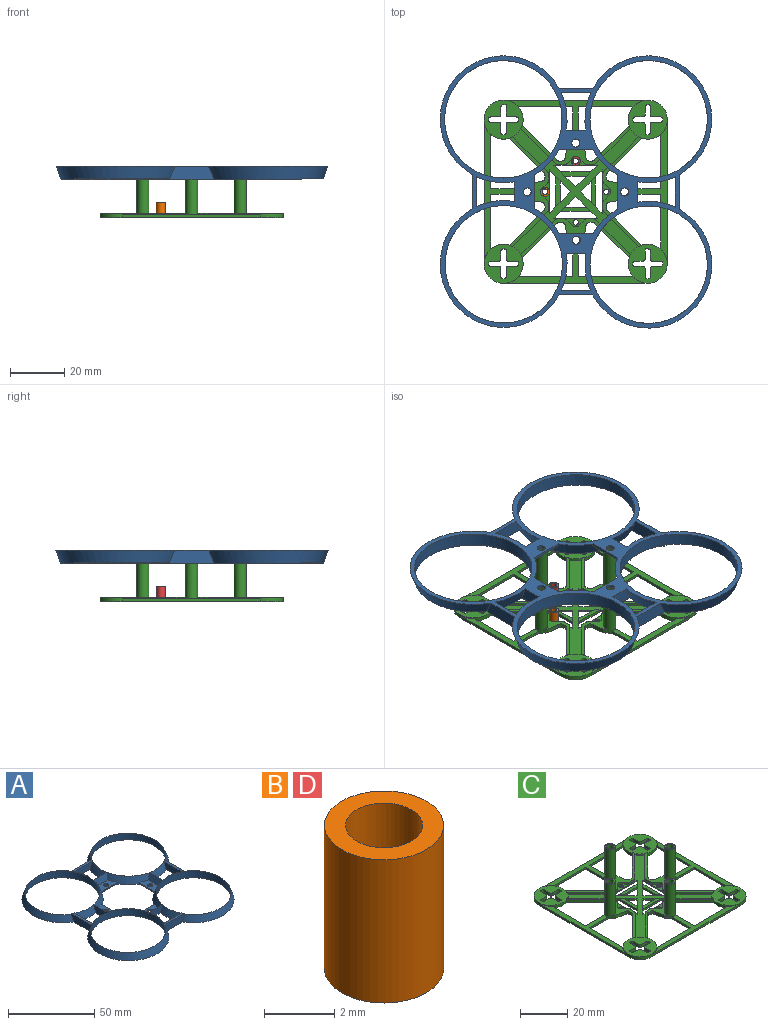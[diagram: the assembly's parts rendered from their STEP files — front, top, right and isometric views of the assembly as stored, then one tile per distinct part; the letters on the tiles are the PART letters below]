
ASSEMBLY  parts=4 mates=3
PART A: 54 faces, bbox 100.6x100.9x5.1 mm
  f0: cylinder r=21.74mm len=43.48mm, axis (0,0,-1), area 657.2mm2, adj f7,f11,f12,f13,f21,f22,f28,f36
  f1: cylinder r=21.74mm len=43.48mm, axis (0,0,-1), area 657.2mm2, adj f5,f6,f7,f8,f9,f17,f25,f26
  f2: cylinder r=21.74mm len=43.48mm, axis (0,0,-1), area 657.2mm2, adj f8,f9,f10,f17,f18,f24,f25,f27
  f3: cylinder r=21.74mm len=43.48mm, axis (0,0,-1), area 657.2mm2, adj f4,f10,f19,f20,f30,f31,f35,f36
  f4: cone r=23.5mm half-angle=20deg, axis (0,0,-1), area 121.3mm2, adj f3,f36,f37,f45,f46,f47,f49,f50
  f5: cone r=23.5mm half-angle=20deg, axis (0,0,-1), area 416mm2, adj f1,f7,f17,f23,f37
  f6: cone r=23.5mm half-angle=20deg, axis (0,0,-1), area 121.3mm2, adj f1,f7,f37,f38,f40,f41,f43,f51
  f7: plane 38.68x36.77mm, normal (0,0,1), area 28.4mm2, adj f0,f1,f5,f6,f14,f15,f16,f22
  f8: plane 16.71x1.51mm, normal (0,0,1), area 23.9mm2, adj f1,f2,f17,f25
  f9: plane 11.13x0.1mm, normal (0,0,1), area 1.1mm2, adj f1,f2,f34,f53
  f10: plane 36.77x27.56mm, normal (0,0,1), area 26.3mm2, adj f2,f3,f18,f19,f27,f29,f30,f35
  f11: plane 10.91x5.01mm, normal (1,0,0), area 45.5mm2, adj f0,f12,f32,f36,f37
  f12: cone r=23.5mm half-angle=20deg, axis (0,0,-1), area 72.2mm2, adj f0,f11,f13,f37
  f13: plane 14.95x5.04mm, normal (-1,0,0), area 65.1mm2, adj f0,f12,f32,f36,f37
  f14: plane 10.97x5.01mm, normal (0,1,0), area 45.5mm2, adj f7,f15,f33,f37
  f15: cone r=23.5mm half-angle=20deg, axis (0,0,-1), area 76.1mm2, adj f7,f14,f16,f37
  f16: plane 15.09x5.04mm, normal (0,-1,0), area 65.1mm2, adj f7,f15,f33,f37
  f17: plane 16.75x5.04mm, normal (-1,0,0), area 74.4mm2, adj f1,f2,f5,f8,f18,f37
  f18: cone r=23.5mm half-angle=20deg, axis (0,0,-1), area 417.6mm2, adj f2,f10,f17,f19,f37
  f19: plane 16.5x5.05mm, normal (0,-1,0), area 72.5mm2, adj f3,f10,f18,f20,f37
  f20: cone r=23.5mm half-angle=20deg, axis (0,0,-1), area 416mm2, adj f3,f19,f21,f36,f37
  f21: plane 16.66x5.05mm, normal (1,0,0), area 73.2mm2, adj f0,f20,f22,f36,f37
  f22: cone r=23.5mm half-angle=20deg, axis (0,0,-1), area 416mm2, adj f0,f7,f21,f23,f37
  f23: plane 16.82x5.05mm, normal (0,1,0), area 73.2mm2, adj f5,f7,f22,f37
  f24: cone r=23.5mm half-angle=20deg, axis (0,0,-1), area 72.2mm2, adj f2,f25,f34,f37
  f25: plane 15.06x5.03mm, normal (1,0,0), area 66.3mm2, adj f1,f2,f8,f24,f26,f37
  f26: cone r=23.5mm half-angle=20deg, axis (0,0,-1), area 72.2mm2, adj f1,f25,f34,f37
  f27: cone r=23.5mm half-angle=20deg, axis (0,0,-1), area 119.8mm2, adj f2,f10,f37,f38,f40,f45,f46,f52
  f28: cone r=23.5mm half-angle=20deg, axis (0,0,-1), area 121.3mm2, adj f0,f7,f37,f41,f43,f47,f49,f50
  f29: cone r=23.5mm half-angle=20deg, axis (0,0,-1), area 75.9mm2, adj f10,f30,f35,f37
  f30: plane 10.96x5.01mm, normal (0,-1,0), area 45.8mm2, adj f3,f10,f29,f31,f37
  f31: cone r=23.5mm half-angle=20deg, axis (0,0,-1), area 72.2mm2, adj f3,f30,f35,f37
  f32: cone r=23.5mm half-angle=20deg, axis (0,0,-1), area 76.1mm2, adj f11,f13,f36,f37
  f33: cone r=23.5mm half-angle=20deg, axis (0,0,-1), area 76.1mm2, adj f7,f14,f16,f37
  f34: plane 11.11x5.01mm, normal (-1,0,0), area 46.8mm2, adj f1,f2,f9,f24,f26,f37
  f35: plane 14.82x5.04mm, normal (0,1,0), area 64.5mm2, adj f3,f10,f29,f31,f37
  f36: plane 36.77x27.56mm, normal (0,0,1), area 26.5mm2, adj f0,f3,f4,f11,f13,f20,f21,f32
  f37: plane 100.84x100.59mm, normal (0,0,-1), area 1324.1mm2, adj f0,f1,f2,f3,f4,f5,f6,f11
  f38: plane 13.52x1mm, normal (1,0,0), area 13.1mm2, adj f6,f27,f37,f40
  f39: cylinder r=1.5mm len=3mm, axis (0,0,-1), area 9.4mm2, adj f37,f40
  f40: plane 13.52x5.75mm, normal (0,0,1), area 55.8mm2, adj f6,f27,f38,f39,f53
  f41: plane 13.26x1mm, normal (0,-1,0), area 12.8mm2, adj f6,f28,f37,f43
  f42: cylinder r=1.5mm len=3mm, axis (0,0,-1), area 9.4mm2, adj f37,f43
  f43: plane 13.26x5.75mm, normal (0,0,1), area 54.3mm2, adj f6,f28,f41,f42,f51
  f44: cylinder r=1.5mm len=3mm, axis (0,0,-1), area 9.4mm2, adj f37,f46
  f45: plane 13.41x1mm, normal (0,1,0), area 13mm2, adj f4,f27,f37,f46
  f46: plane 13.41x5.75mm, normal (0,0,1), area 54.9mm2, adj f4,f27,f44,f45,f52
  f47: plane 13.26x1mm, normal (-1,0,0), area 12.8mm2, adj f4,f28,f37,f49
  f48: cylinder r=1.5mm len=3mm, axis (0,0,-1), area 9.4mm2, adj f37,f49
  f49: plane 13.26x5.75mm, normal (0,0,1), area 54.3mm2, adj f4,f28,f47,f48,f50
  f50: plane 11.01x4.06mm, normal (-0.93,0,0.36), area 42.1mm2, adj f0,f4,f28,f36,f49
  f51: plane 11.05x4.06mm, normal (0,-0.93,0.36), area 42.1mm2, adj f6,f7,f28,f43
  f52: plane 11.06x4.06mm, normal (0,0.93,0.36), area 42.4mm2, adj f3,f4,f10,f27,f46
  f53: plane 11.21x4.05mm, normal (0.93,0,0.36), area 43.2mm2, adj f1,f2,f6,f9,f27,f40
PART B: 4 faces, bbox 3.4x3.4x5 mm
  f0: cylinder r=1.1mm len=5mm, axis (0,0,-1), area 34.6mm2, adj f2,f3
  f1: cylinder r=1.7mm len=5mm, axis (0,0,-1), area 53.4mm2, adj f2,f3
  f2: plane 3.4x3.4mm, normal (0,0,1), area 5.3mm2, adj f0,f1
  f3: plane 3.4x3.4mm, normal (0,0,-1), area 5.3mm2, adj f0,f1
PART C: 299 faces, bbox 67.8x67.8x18 mm
  f0: cylinder r=7.23mm len=14.46mm, axis (0,0,-1), area 47.5mm2, adj f33,f70,f77,f94,f275,f276,f280,f282
  f1: cylinder r=2.25mm len=18mm, axis (0,0,-1), area 237.7mm2, adj f32,f36,f37,f77,f78,f281,f285,f286
  f2: plane 4.02x4.02mm, normal (0.71,0.71,0), area 3.4mm2, adj f11,f77,f165,f272
  f3: plane 2.5x2.5mm, normal (0.71,-0.71,0), area 2.1mm2, adj f22,f77,f165,f273
  f4: plane 2.5x2.5mm, normal (-0.71,-0.71,0), area 2.1mm2, adj f13,f77,f165,f268
  f5: plane 4.02x4.02mm, normal (0.71,-0.71,0), area 3.4mm2, adj f12,f77,f165,f267
  f6: plane 2.5x2.5mm, normal (-0.71,0.71,0), area 2.1mm2, adj f17,f77,f165,f263
  f7: plane 4.02x4.02mm, normal (-0.71,-0.71,0), area 3.4mm2, adj f16,f77,f165,f262
  f8: plane 2.5x2.5mm, normal (-0.71,0.71,0), area 2.1mm2, adj f27,f77,f165,f258
  f9: plane 4.02x4.02mm, normal (0.71,0.71,0), area 3.4mm2, adj f14,f77,f165,f257
  f10: plane 2.5x2.5mm, normal (0.71,0.71,0), area 2.1mm2, adj f22,f77,f165,f273
  f11: plane 4.02x4.02mm, normal (0.71,-0.71,0), area 3.4mm2, adj f2,f77,f165,f272
  f12: plane 4.02x4.02mm, normal (-0.71,-0.71,0), area 3.4mm2, adj f5,f77,f165,f267
  f13: plane 16.1x0.6mm, normal (0,1,0), area 9.7mm2, adj f4,f26,f77,f165
  f14: plane 4.02x4.02mm, normal (-0.71,0.71,0), area 3.4mm2, adj f9,f77,f165,f257
  f15: plane 2.5x2.5mm, normal (0.71,0.71,0), area 2.1mm2, adj f27,f77,f165,f258
  f16: plane 4.02x4.02mm, normal (-0.71,0.71,0), area 3.4mm2, adj f7,f77,f165,f262
  f17: plane 16.1x0.6mm, normal (1,0,0), area 9.7mm2, adj f6,f28,f77,f165
  f18: cylinder r=7.23mm len=1.16mm, axis (0,0,-1), area 0.1mm2, adj f42,f76,f122,f158
  f19: cylinder r=7.23mm len=1.19mm, axis (0,0,-1), area 0.1mm2, adj f30,f52,f136,f137
  f20: cylinder r=7.23mm len=1.16mm, axis (0,0,-1), area 0.1mm2, adj f31,f62,f108,f144
  f21: cylinder r=1mm len=2mm, axis (0,0,-1), area 3.8mm2, adj f77,f165
  f22: plane 16.1x0.6mm, normal (-1,0,0), area 9.7mm2, adj f3,f10,f77,f165
  f23: cylinder r=1mm len=2mm, axis (0,0,-1), area 3.8mm2, adj f77,f165
  f24: cylinder r=1mm len=2mm, axis (0,0,-1), area 3.8mm2, adj f77,f165
  f25: cylinder r=1mm len=2mm, axis (0,0,-1), area 3.8mm2, adj f77,f165
  f26: plane 2.5x2.5mm, normal (0.71,-0.71,0), area 2.1mm2, adj f13,f77,f165,f268
  f27: plane 16.1x0.6mm, normal (0,-1,0), area 9.7mm2, adj f8,f15,f77,f165
  f28: plane 2.5x2.5mm, normal (-0.71,-0.71,0), area 2.1mm2, adj f17,f77,f165,f263
  f29: cylinder r=7.23mm len=1.19mm, axis (0,0,-1), area 0.1mm2, adj f31,f70,f94,f149
  f30: plane 40.62x14.52mm, normal (0,0,1), area 90.9mm2, adj f19,f52,f53,f54,f55,f56,f57,f58
  f31: plane 40.61x14.49mm, normal (0,0,1), area 89.8mm2, adj f20,f29,f62,f63,f64,f65,f66,f67
  f32: plane 40.61x14.52mm, normal (0,0,1), area 91mm2, adj f1,f33,f34,f35,f36,f37,f38,f39
  f33: plane 12.73x12.73mm, normal (-0.71,-0.71,0), area 28.8mm2, adj f0,f32,f74,f77,f186
  f34: plane 1.6x0.71mm, normal (-1,0,0), area 1.1mm2, adj f32,f77,f186,f187
  f35: plane 4.91x1.6mm, normal (-0.15,0.99,0), area 7.9mm2, adj f32,f77,f187,f191
  f36: plane 1.6x0.64mm, normal (-0.71,0.7,0), area 1.4mm2, adj f1,f32,f77,f191
  f37: plane 1.6x0.64mm, normal (-0.71,-0.7,0), area 1.4mm2, adj f1,f32,f77,f192
  f38: plane 4.91x1.6mm, normal (-0.15,-0.99,0), area 7.9mm2, adj f32,f77,f192,f193
  f39: plane 1.6x0.71mm, normal (-1,0,0), area 1.1mm2, adj f32,f77,f193,f194
  f40: plane 12.73x12.73mm, normal (-0.71,0.71,0), area 28.8mm2, adj f32,f41,f77,f109,f194
  f41: cylinder r=7.23mm len=1.23mm, axis (0,0,-1), area 0.1mm2, adj f32,f40,f122,f156
  f42: plane 12.7x12.7mm, normal (0.71,-0.71,0), area 28.7mm2, adj f18,f76,f77,f109,f195
  f43: plane 1.6x0.76mm, normal (0,-1,0), area 1.2mm2, adj f76,f77,f195,f196
  f44: plane 4.91x1.6mm, normal (-0.99,-0.15,0), area 7.9mm2, adj f76,f77,f196,f197
  f45: plane 1.6x0.64mm, normal (-0.7,-0.71,0), area 1.4mm2, adj f46,f76,f77,f197
  f46: cylinder r=2.25mm len=18mm, axis (0,0,-1), area 237.7mm2, adj f45,f47,f76,f77,f81,f293,f297,f298
  f47: plane 1.6x0.64mm, normal (0.7,-0.71,0), area 1.4mm2, adj f46,f76,f77,f198
  f48: plane 4.91x1.6mm, normal (0.99,-0.15,0), area 7.9mm2, adj f76,f77,f198,f199
  f49: plane 1.6x0.71mm, normal (0,-1,0), area 1.1mm2, adj f76,f77,f199,f200
  f50: plane 12.73x12.73mm, normal (-0.71,-0.71,0), area 28.8mm2, adj f51,f76,f77,f123,f200
  f51: cylinder r=7.23mm len=1.2mm, axis (0,0,-1), area 0.1mm2, adj f50,f76,f136,f163
  f52: plane 12.7x12.7mm, normal (0.71,0.71,0), area 28.7mm2, adj f19,f30,f77,f123,f201
  f53: plane 1.6x0.76mm, normal (1,0,0), area 1.2mm2, adj f30,f77,f201,f207
  f54: plane 4.91x1.6mm, normal (0.15,-0.99,0), area 7.9mm2, adj f30,f77,f207,f208
  f55: plane 1.6x0.64mm, normal (0.71,-0.7,0), area 1.4mm2, adj f30,f56,f77,f208
  f56: cylinder r=2.25mm len=18mm, axis (0,0,-1), area 237.7mm2, adj f30,f55,f57,f77,f80,f287,f291,f292
  f57: plane 1.6x0.64mm, normal (0.71,0.7,0), area 1.4mm2, adj f30,f56,f77,f206
  f58: plane 4.91x1.6mm, normal (0.15,0.99,0), area 7.9mm2, adj f30,f77,f205,f206
  f59: plane 1.6x0.71mm, normal (1,0,0), area 1.1mm2, adj f30,f77,f190,f205
  f60: plane 12.73x12.73mm, normal (0.71,-0.71,0), area 28.8mm2, adj f30,f61,f77,f95,f190
  f61: cylinder r=7.23mm len=1.23mm, axis (0,0,-1), area 0.1mm2, adj f30,f60,f108,f142
  f62: plane 12.7x12.7mm, normal (-0.71,0.71,0), area 28.7mm2, adj f20,f31,f77,f95,f189
  f63: plane 1.6x0.76mm, normal (0,1,0), area 1.2mm2, adj f31,f77,f189,f203
  f64: plane 4.91x1.6mm, normal (0.99,0.15,0), area 7.9mm2, adj f31,f77,f203,f204
  f65: plane 1.6x0.64mm, normal (0.7,0.71,0), area 1.4mm2, adj f31,f66,f77,f204
  f66: cylinder r=2.25mm len=18mm, axis (0,0,-1), area 237.7mm2, adj f31,f65,f67,f77,f79,f277,f278,f280
  f67: plane 1.6x0.64mm, normal (-0.7,0.71,0), area 1.4mm2, adj f31,f66,f77,f202
  f68: plane 4.91x1.6mm, normal (-0.99,0.15,0), area 7.9mm2, adj f31,f77,f188,f202
  f69: plane 1.6x0.76mm, normal (0,1,0), area 1.2mm2, adj f31,f77,f185,f188
  f70: plane 12.7x12.7mm, normal (0.71,0.71,0), area 28.7mm2, adj f0,f29,f31,f77,f185
  f71: cylinder r=1.5mm len=18mm, axis (0,0,-1), area 169.6mm2, adj f77,f79
  f72: cylinder r=1.5mm len=18mm, axis (0,0,-1), area 169.6mm2, adj f77,f81
  f73: cylinder r=1.5mm len=18mm, axis (0,0,-1), area 169.6mm2, adj f77,f80
  f74: cylinder r=7.23mm len=1.2mm, axis (0,0,-1), area 0.1mm2, adj f32,f33,f94,f151
  f75: cylinder r=1.5mm len=18mm, axis (0,0,-1), area 169.6mm2, adj f77,f78
  f76: plane 40.59x14.52mm, normal (0,0,1), area 89.6mm2, adj f18,f42,f43,f44,f45,f46,f47,f48
  f77: plane 67.84x67.84mm, normal (0,0,-1), area 1962.7mm2, adj f0,f1,f2,f3,f4,f5,f6,f7
  f78: plane 4.5x4.5mm, normal (0,0,1), area 8.8mm2, adj f1,f75
  f79: plane 4.5x4.5mm, normal (0,0,1), area 8.8mm2, adj f66,f71
  f80: plane 4.5x4.5mm, normal (0,0,1), area 8.8mm2, adj f56,f73
  f81: plane 4.5x4.5mm, normal (0,0,1), area 8.8mm2, adj f46,f72
  f82: plane 3.1x1.5mm, normal (0,1,0), area 4.6mm2, adj f77,f94,f209,f219
  f83: plane 3.1x1.5mm, normal (-1,0,0), area 4.6mm2, adj f77,f94,f218,f219
  f84: plane 1.5x0.6mm, normal (0,1,0), area 0.9mm2, adj f77,f94,f217,f218
  f85: plane 3.1x1.5mm, normal (1,0,0), area 4.6mm2, adj f77,f94,f216,f217
  f86: plane 3.1x1.5mm, normal (0,1,0), area 4.7mm2, adj f77,f94,f215,f216
  f87: plane 1.5x0.6mm, normal (1,0,0), area 0.9mm2, adj f77,f94,f214,f215
  f88: plane 3.1x1.5mm, normal (0,-1,0), area 4.7mm2, adj f77,f94,f213,f214
  f89: plane 3.1x1.5mm, normal (1,0,0), area 4.7mm2, adj f77,f94,f212,f213
  f90: plane 1.5x1.3mm, normal (0,-1,0), area 2mm2, adj f77,f91,f94,f212
  f91: plane 3.8x1.5mm, normal (-1,0,0), area 5.7mm2, adj f77,f90,f94,f211
  f92: plane 3.1x1.5mm, normal (0,-1,0), area 4.6mm2, adj f77,f94,f210,f211
  f93: plane 1.5x0.6mm, normal (-1,0,0), area 0.9mm2, adj f77,f94,f209,f210
  f94: plane 14.46x14.46mm, normal (0,0,1), area 124.5mm2, adj f0,f29,f74,f82,f83,f84,f85,f86
  f95: cylinder r=7.23mm len=14.46mm, axis (0,0,-1), area 47.5mm2, adj f60,f62,f77,f108,f275,f279,f280,f289
  f96: plane 3.1x1.5mm, normal (1,0,0), area 4.6mm2, adj f77,f108,f220,f231
  f97: plane 3.1x1.5mm, normal (0,1,0), area 4.6mm2, adj f77,f108,f230,f231
  f98: plane 1.5x0.6mm, normal (1,0,0), area 0.9mm2, adj f77,f108,f229,f230
  f99: plane 3.1x1.5mm, normal (0,-1,0), area 4.6mm2, adj f77,f108,f228,f229
  f100: plane 3.1x1.5mm, normal (1,0,0), area 4.7mm2, adj f77,f108,f227,f228
  f101: plane 1.5x0.6mm, normal (0,-1,0), area 0.9mm2, adj f77,f108,f226,f227
  f102: plane 3.1x1.5mm, normal (-1,0,0), area 4.7mm2, adj f77,f108,f225,f226
  f103: plane 3.1x1.5mm, normal (0,-1,0), area 4.7mm2, adj f77,f108,f224,f225
  f104: plane 1.5x0.6mm, normal (-1,0,0), area 0.9mm2, adj f77,f108,f223,f224
  f105: plane 3.1x1.5mm, normal (0,1,0), area 4.7mm2, adj f77,f108,f222,f223
  f106: plane 3.1x1.5mm, normal (-1,0,0), area 4.6mm2, adj f77,f108,f221,f222
  f107: plane 1.5x0.6mm, normal (0,1,0), area 0.9mm2, adj f77,f108,f220,f221
  f108: plane 14.46x14.46mm, normal (0,0,1), area 124.6mm2, adj f20,f61,f95,f96,f97,f98,f99,f100
  f109: cylinder r=7.23mm len=14.46mm, axis (0,0,-1), area 47.5mm2, adj f40,f42,f77,f122,f283,f284,f286,f294
  f110: plane 3.1x1.5mm, normal (0,1,0), area 4.7mm2, adj f77,f122,f232,f243
  f111: plane 1.5x0.6mm, normal (1,0,0), area 0.9mm2, adj f77,f122,f232,f233
  f112: plane 3.1x1.5mm, normal (0,-1,0), area 4.7mm2, adj f77,f122,f233,f234
  f113: plane 3.1x1.5mm, normal (1,0,0), area 4.6mm2, adj f77,f122,f234,f235
  f114: plane 1.5x0.6mm, normal (0,-1,0), area 0.9mm2, adj f77,f122,f235,f236
  f115: plane 3.1x1.5mm, normal (-1,0,0), area 4.6mm2, adj f77,f122,f236,f237
  f116: plane 3.1x1.5mm, normal (0,-1,0), area 4.6mm2, adj f77,f122,f237,f238
  f117: plane 1.5x0.6mm, normal (-1,0,0), area 0.9mm2, adj f77,f122,f238,f239
  f118: plane 3.1x1.5mm, normal (0,1,0), area 4.6mm2, adj f77,f122,f239,f240
  f119: plane 3.1x1.5mm, normal (-1,0,0), area 4.7mm2, adj f77,f122,f240,f241
  f120: plane 1.5x0.6mm, normal (0,1,0), area 0.9mm2, adj f77,f122,f241,f242
  f121: plane 3.1x1.5mm, normal (1,0,0), area 4.7mm2, adj f77,f122,f242,f243
  f122: plane 14.46x14.46mm, normal (0,0,1), area 124.6mm2, adj f18,f41,f109,f110,f111,f112,f113,f114
  f123: cylinder r=7.23mm len=14.46mm, axis (0,0,-1), area 47.5mm2, adj f50,f52,f77,f136,f288,f289,f292,f295
  f124: plane 3.1x1.5mm, normal (-1,0,0), area 4.7mm2, adj f77,f136,f244,f254
  f125: plane 1.5x0.6mm, normal (0,1,0), area 0.9mm2, adj f77,f136,f253,f254
  f126: plane 3.1x1.5mm, normal (1,0,0), area 4.7mm2, adj f77,f136,f252,f253
  f127: plane 3.1x1.5mm, normal (0,1,0), area 4.6mm2, adj f77,f136,f251,f252
  f128: plane 1.5x0.6mm, normal (1,0,0), area 0.9mm2, adj f77,f136,f250,f251
  f129: plane 3.1x1.5mm, normal (0,-1,0), area 4.6mm2, adj f77,f136,f249,f250
  f130: plane 3.8x1.5mm, normal (1,0,0), area 5.7mm2, adj f77,f131,f136,f249
  f131: plane 1.5x1.3mm, normal (0,-1,0), area 2mm2, adj f77,f130,f136,f248
  f132: plane 3.1x1.5mm, normal (-1,0,0), area 4.6mm2, adj f77,f136,f247,f248
  f133: plane 3.1x1.5mm, normal (0,-1,0), area 4.7mm2, adj f77,f136,f246,f247
  f134: plane 1.5x0.6mm, normal (-1,0,0), area 0.9mm2, adj f77,f136,f245,f246
  f135: plane 3.1x1.5mm, normal (0,1,0), area 4.7mm2, adj f77,f136,f244,f245
  f136: plane 14.46x14.46mm, normal (0,0,1), area 124.5mm2, adj f19,f51,f123,f124,f125,f126,f127,f128
  f137: plane 12.86x12.86mm, normal (-0.71,-0.71,0), area 18.2mm2, adj f19,f30,f164,f165,f167
  f138: plane 2.11x1mm, normal (-1,0,0), area 2.1mm2, adj f30,f165,f167,f180
  f139: plane 2.16x2.16mm, normal (-0.71,0.71,0), area 3.1mm2, adj f30,f165,f180,f183
  f140: plane 2.16x2.16mm, normal (-0.71,-0.71,0), area 3.1mm2, adj f30,f165,f169,f183
  f141: plane 2.13x1mm, normal (-1,0,0), area 2.1mm2, adj f30,f165,f169,f170
  f142: plane 12.86x12.86mm, normal (-0.71,0.71,0), area 18.2mm2, adj f30,f61,f143,f165,f170
  f143: cylinder r=7.23mm len=3.01mm, axis (0,0,1), area 3.9mm2, adj f108,f142,f144,f165
  f144: plane 12.89x12.89mm, normal (0.71,-0.71,0), area 18.2mm2, adj f20,f31,f143,f165,f168
  f145: plane 2.7x1mm, normal (0,-1,0), area 2.7mm2, adj f31,f146,f165,f168
  f146: plane 2.58x2.58mm, normal (-0.71,-0.71,0), area 3.6mm2, adj f31,f145,f165,f182
  f147: plane 2.14x2.14mm, normal (0.71,-0.71,0), area 3mm2, adj f31,f165,f181,f182
  f148: plane 2.14x1mm, normal (0,-1,0), area 2.1mm2, adj f31,f165,f174,f181
  f149: plane 12.86x12.86mm, normal (-0.71,-0.71,0), area 18.2mm2, adj f29,f31,f150,f165,f174
  f150: cylinder r=7.23mm len=3.01mm, axis (0,0,1), area 3.9mm2, adj f94,f149,f151,f165
  f151: plane 12.89x12.89mm, normal (0.71,0.71,0), area 18.2mm2, adj f32,f74,f150,f165,f173
  f152: plane 2.09x1mm, normal (1,0,0), area 2.1mm2, adj f32,f165,f173,f176
  f153: plane 2.15x2.15mm, normal (0.71,-0.71,0), area 3mm2, adj f32,f165,f176,f177
  f154: plane 2.15x2.15mm, normal (0.71,0.71,0), area 3mm2, adj f32,f165,f175,f177
  f155: plane 2.12x1mm, normal (1,0,0), area 2.1mm2, adj f32,f165,f172,f175
  f156: plane 12.86x12.86mm, normal (0.71,-0.71,0), area 18.2mm2, adj f32,f41,f157,f165,f172
  f157: cylinder r=7.23mm len=3.01mm, axis (0,0,1), area 3.9mm2, adj f122,f156,f158,f165
  f158: plane 12.89x12.89mm, normal (-0.71,0.71,0), area 18.2mm2, adj f18,f76,f157,f165,f171
  f159: plane 2.07x1mm, normal (0,1,0), area 2.1mm2, adj f76,f165,f171,f178
  f160: plane 2.16x2.16mm, normal (0.71,0.71,0), area 3.1mm2, adj f76,f165,f178,f184
  f161: plane 2.16x2.16mm, normal (-0.71,0.71,0), area 3.1mm2, adj f76,f165,f179,f184
  f162: plane 2.06x1mm, normal (0,1,0), area 2.1mm2, adj f76,f165,f166,f179
  f163: plane 12.89x12.89mm, normal (0.71,0.71,0), area 18.2mm2, adj f51,f76,f164,f165,f166
  f164: cylinder r=7.23mm len=3.01mm, axis (0,0,1), area 3.9mm2, adj f136,f137,f163,f165
  f165: plane 46.65x46.62mm, normal (0,0,1), area 478.8mm2, adj f2,f3,f4,f5,f6,f7,f8,f9
  f166: cylinder r=1.5mm len=1.06mm, axis (0,0,1), area 1.2mm2, adj f76,f162,f163,f165
  f167: cylinder r=1.5mm len=1.06mm, axis (0,0,-1), area 1.2mm2, adj f30,f137,f138,f165
  f168: cylinder r=1.5mm len=1.06mm, axis (0,0,1), area 1.2mm2, adj f31,f144,f145,f165
  f169: cylinder r=1.5mm len=1.06mm, axis (0,0,-1), area 1.2mm2, adj f30,f140,f141,f165
  f170: cylinder r=1.5mm len=1.06mm, axis (0,0,1), area 1.2mm2, adj f30,f141,f142,f165
  f171: cylinder r=1.5mm len=1.06mm, axis (0,0,-1), area 1.2mm2, adj f76,f158,f159,f165
  f172: cylinder r=1.5mm len=1.06mm, axis (0,0,-1), area 1.2mm2, adj f32,f155,f156,f165
  f173: cylinder r=1.5mm len=1.06mm, axis (0,0,-1), area 1.2mm2, adj f32,f151,f152,f165
  f174: cylinder r=1.5mm len=1.06mm, axis (0,0,1), area 1.2mm2, adj f31,f148,f149,f165
  f175: cylinder r=1.5mm len=1.06mm, axis (0,0,1), area 1.2mm2, adj f32,f154,f155,f165
  f176: cylinder r=1.5mm len=1.06mm, axis (0,0,1), area 1.2mm2, adj f32,f152,f153,f165
  f177: cylinder r=1.5mm len=2.12mm, axis (0,0,-1), area 2.4mm2, adj f32,f153,f154,f165
  f178: cylinder r=1.5mm len=1.06mm, axis (0,0,1), area 1.2mm2, adj f76,f159,f160,f165
  f179: cylinder r=1.5mm len=1.06mm, axis (0,0,1), area 1.2mm2, adj f76,f161,f162,f165
  f180: cylinder r=1.5mm len=1.06mm, axis (0,0,-1), area 1.2mm2, adj f30,f138,f139,f165
  f181: cylinder r=1.5mm len=1.06mm, axis (0,0,-1), area 1.2mm2, adj f31,f147,f148,f165
  f182: cylinder r=1.5mm len=2.12mm, axis (0,0,-1), area 2.4mm2, adj f31,f146,f147,f165
  f183: cylinder r=1.5mm len=2.12mm, axis (0,0,-1), area 2.4mm2, adj f30,f139,f140,f165
  f184: cylinder r=1.5mm len=2.12mm, axis (0,0,-1), area 2.4mm2, adj f76,f160,f161,f165
  f185: cylinder r=1.5mm len=1.6mm, axis (0,0,1), area 1.9mm2, adj f31,f69,f70,f77
  f186: cylinder r=1.5mm len=1.6mm, axis (0,0,-1), area 1.9mm2, adj f32,f33,f34,f77
  f187: cylinder r=1.5mm len=1.6mm, axis (0,0,1), area 3.4mm2, adj f32,f34,f35,f77
  f188: cylinder r=1.5mm len=1.6mm, axis (0,0,1), area 3.4mm2, adj f31,f68,f69,f77
  f189: cylinder r=1.5mm len=1.6mm, axis (0,0,-1), area 1.9mm2, adj f31,f62,f63,f77
  f190: cylinder r=1.5mm len=1.6mm, axis (0,0,-1), area 1.9mm2, adj f30,f59,f60,f77
  f191: cylinder r=1.5mm len=1.6mm, axis (0,0,-1), area 1.6mm2, adj f32,f35,f36,f77
  f192: cylinder r=1.5mm len=1.6mm, axis (0,0,-1), area 1.6mm2, adj f32,f37,f38,f77
  f193: cylinder r=1.5mm len=1.6mm, axis (0,0,-1), area 3.4mm2, adj f32,f38,f39,f77
  f194: cylinder r=1.5mm len=1.6mm, axis (0,0,1), area 1.9mm2, adj f32,f39,f40,f77
  f195: cylinder r=1.5mm len=1.6mm, axis (0,0,1), area 1.9mm2, adj f42,f43,f76,f77
  f196: cylinder r=1.5mm len=1.6mm, axis (0,0,1), area 3.4mm2, adj f43,f44,f76,f77
  f197: cylinder r=1.5mm len=1.6mm, axis (0,0,-1), area 1.6mm2, adj f44,f45,f76,f77
  f198: cylinder r=1.5mm len=1.6mm, axis (0,0,-1), area 1.6mm2, adj f47,f48,f76,f77
  f199: cylinder r=1.5mm len=1.6mm, axis (0,0,-1), area 3.4mm2, adj f48,f49,f76,f77
  f200: cylinder r=1.5mm len=1.6mm, axis (0,0,1), area 1.9mm2, adj f49,f50,f76,f77
  f201: cylinder r=1.5mm len=1.6mm, axis (0,0,-1), area 1.9mm2, adj f30,f52,f53,f77
  f202: cylinder r=1.5mm len=1.6mm, axis (0,0,-1), area 1.6mm2, adj f31,f67,f68,f77
  f203: cylinder r=1.5mm len=1.6mm, axis (0,0,-1), area 3.4mm2, adj f31,f63,f64,f77
  f204: cylinder r=1.5mm len=1.6mm, axis (0,0,-1), area 1.6mm2, adj f31,f64,f65,f77
  f205: cylinder r=1.5mm len=1.6mm, axis (0,0,1), area 3.4mm2, adj f30,f58,f59,f77
  f206: cylinder r=1.5mm len=1.6mm, axis (0,0,-1), area 1.6mm2, adj f30,f57,f58,f77
  f207: cylinder r=1.5mm len=1.6mm, axis (0,0,-1), area 3.4mm2, adj f30,f53,f54,f77
  f208: cylinder r=1.5mm len=1.6mm, axis (0,0,-1), area 1.6mm2, adj f30,f54,f55,f77
  f209: cylinder r=0.7mm len=1.5mm, axis (0,0,-1), area 1.6mm2, adj f77,f82,f93,f94
  f210: cylinder r=0.7mm len=1.5mm, axis (0,0,1), area 1.6mm2, adj f77,f92,f93,f94
  f211: cylinder r=0.7mm len=1.5mm, axis (0,0,-1), area 1.6mm2, adj f77,f91,f92,f94
  f212: cylinder r=0.7mm len=1.5mm, axis (0,0,-1), area 1.6mm2, adj f77,f89,f90,f94
  f213: cylinder r=0.7mm len=1.5mm, axis (0,0,1), area 1.6mm2, adj f77,f88,f89,f94
  f214: cylinder r=0.7mm len=1.5mm, axis (0,0,-1), area 1.6mm2, adj f77,f87,f88,f94
  f215: cylinder r=0.7mm len=1.5mm, axis (0,0,1), area 1.6mm2, adj f77,f86,f87,f94
  f216: cylinder r=0.7mm len=1.5mm, axis (0,0,-1), area 1.6mm2, adj f77,f85,f86,f94
  f217: cylinder r=0.7mm len=1.5mm, axis (0,0,1), area 1.6mm2, adj f77,f84,f85,f94
  f218: cylinder r=0.7mm len=1.5mm, axis (0,0,-1), area 1.6mm2, adj f77,f83,f84,f94
  f219: cylinder r=0.7mm len=1.5mm, axis (0,0,1), area 1.6mm2, adj f77,f82,f83,f94
  f220: cylinder r=0.7mm len=1.5mm, axis (0,0,-1), area 1.6mm2, adj f77,f96,f107,f108
  f221: cylinder r=0.7mm len=1.5mm, axis (0,0,1), area 1.6mm2, adj f77,f106,f107,f108
  f222: cylinder r=0.7mm len=1.5mm, axis (0,0,-1), area 1.6mm2, adj f77,f105,f106,f108
  f223: cylinder r=0.7mm len=1.5mm, axis (0,0,1), area 1.6mm2, adj f77,f104,f105,f108
  f224: cylinder r=0.7mm len=1.5mm, axis (0,0,-1), area 1.6mm2, adj f77,f103,f104,f108
  f225: cylinder r=0.7mm len=1.5mm, axis (0,0,1), area 1.6mm2, adj f77,f102,f103,f108
  f226: cylinder r=0.7mm len=1.5mm, axis (0,0,-1), area 1.6mm2, adj f77,f101,f102,f108
  f227: cylinder r=0.7mm len=1.5mm, axis (0,0,1), area 1.6mm2, adj f77,f100,f101,f108
  f228: cylinder r=0.7mm len=1.5mm, axis (0,0,-1), area 1.6mm2, adj f77,f99,f100,f108
  f229: cylinder r=0.7mm len=1.5mm, axis (0,0,1), area 1.6mm2, adj f77,f98,f99,f108
  f230: cylinder r=0.7mm len=1.5mm, axis (0,0,-1), area 1.6mm2, adj f77,f97,f98,f108
  f231: cylinder r=0.7mm len=1.5mm, axis (0,0,1), area 1.6mm2, adj f77,f96,f97,f108
  f232: cylinder r=0.7mm len=1.5mm, axis (0,0,-1), area 1.6mm2, adj f77,f110,f111,f122
  f233: cylinder r=0.7mm len=1.5mm, axis (0,0,1), area 1.6mm2, adj f77,f111,f112,f122
  f234: cylinder r=0.7mm len=1.5mm, axis (0,0,-1), area 1.6mm2, adj f77,f112,f113,f122
  f235: cylinder r=0.7mm len=1.5mm, axis (0,0,1), area 1.6mm2, adj f77,f113,f114,f122
  f236: cylinder r=0.7mm len=1.5mm, axis (0,0,-1), area 1.6mm2, adj f77,f114,f115,f122
  f237: cylinder r=0.7mm len=1.5mm, axis (0,0,1), area 1.6mm2, adj f77,f115,f116,f122
  f238: cylinder r=0.7mm len=1.5mm, axis (0,0,-1), area 1.6mm2, adj f77,f116,f117,f122
  f239: cylinder r=0.7mm len=1.5mm, axis (0,0,1), area 1.6mm2, adj f77,f117,f118,f122
  f240: cylinder r=0.7mm len=1.5mm, axis (0,0,-1), area 1.6mm2, adj f77,f118,f119,f122
  f241: cylinder r=0.7mm len=1.5mm, axis (0,0,1), area 1.6mm2, adj f77,f119,f120,f122
  f242: cylinder r=0.7mm len=1.5mm, axis (0,0,-1), area 1.6mm2, adj f77,f120,f121,f122
  f243: cylinder r=0.7mm len=1.5mm, axis (0,0,1), area 1.6mm2, adj f77,f110,f121,f122
  f244: cylinder r=0.7mm len=1.5mm, axis (0,0,1), area 1.6mm2, adj f77,f124,f135,f136
  f245: cylinder r=0.7mm len=1.5mm, axis (0,0,-1), area 1.6mm2, adj f77,f134,f135,f136
  f246: cylinder r=0.7mm len=1.5mm, axis (0,0,1), area 1.6mm2, adj f77,f133,f134,f136
  f247: cylinder r=0.7mm len=1.5mm, axis (0,0,-1), area 1.6mm2, adj f77,f132,f133,f136
  f248: cylinder r=0.7mm len=1.5mm, axis (0,0,1), area 1.6mm2, adj f77,f131,f132,f136
  f249: cylinder r=0.7mm len=1.5mm, axis (0,0,1), area 1.6mm2, adj f77,f129,f130,f136
  f250: cylinder r=0.7mm len=1.5mm, axis (0,0,-1), area 1.6mm2, adj f77,f128,f129,f136
  f251: cylinder r=0.7mm len=1.5mm, axis (0,0,1), area 1.6mm2, adj f77,f127,f128,f136
  f252: cylinder r=0.7mm len=1.5mm, axis (0,0,-1), area 1.6mm2, adj f77,f126,f127,f136
  f253: cylinder r=0.7mm len=1.5mm, axis (0,0,1), area 1.6mm2, adj f77,f125,f126,f136
  f254: cylinder r=0.7mm len=1.5mm, axis (0,0,-1), area 1.6mm2, adj f77,f124,f125,f136
  f255: plane 1.52x1.52mm, normal (0.71,-0.71,0), area 0.9mm2, adj f165,f257,f258,f259
  f256: plane 1.52x1.52mm, normal (-0.71,-0.71,0), area 0.9mm2, adj f165,f257,f258,f259
  f257: plane 8.05x1mm, normal (0,-1,0), area 8mm2, adj f9,f14,f77,f255,f256,f259
  f258: plane 11.1x1mm, normal (0,1,0), area 11.1mm2, adj f8,f15,f77,f255,f256,f259
  f259: plane 11.1x1.52mm, normal (0,0,1), area 14.6mm2, adj f255,f256,f257,f258
  f260: plane 1.52x1.52mm, normal (0.71,-0.71,0), area 0.9mm2, adj f165,f262,f263,f264
  f261: plane 1.52x1.52mm, normal (0.71,0.71,0), area 0.9mm2, adj f165,f262,f263,f264
  f262: plane 8.05x1mm, normal (1,0,0), area 8mm2, adj f7,f16,f77,f260,f261,f264
  f263: plane 11.1x1mm, normal (-1,0,0), area 11.1mm2, adj f6,f28,f77,f260,f261,f264
  f264: plane 11.1x1.52mm, normal (0,0,1), area 14.6mm2, adj f260,f261,f262,f263
  f265: plane 1.52x1.52mm, normal (0.71,0.71,0), area 0.9mm2, adj f165,f267,f268,f269
  f266: plane 1.52x1.52mm, normal (-0.71,0.71,0), area 0.9mm2, adj f165,f267,f268,f269
  f267: plane 8.05x1mm, normal (0,1,0), area 8mm2, adj f5,f12,f77,f265,f266,f269
  f268: plane 11.1x1mm, normal (0,-1,0), area 11.1mm2, adj f4,f26,f77,f265,f266,f269
  f269: plane 11.1x1.52mm, normal (0,0,1), area 14.6mm2, adj f265,f266,f267,f268
  f270: plane 1.52x1.52mm, normal (-0.71,-0.71,0), area 0.9mm2, adj f165,f272,f273,f274
  f271: plane 1.52x1.52mm, normal (-0.71,0.71,0), area 0.9mm2, adj f165,f272,f273,f274
  f272: plane 8.05x1mm, normal (-1,0,0), area 8mm2, adj f2,f11,f77,f270,f271,f274
  f273: plane 11.1x1mm, normal (1,0,0), area 11.1mm2, adj f3,f10,f77,f270,f271,f274
  f274: plane 11.1x1.52mm, normal (0,0,1), area 14.6mm2, adj f270,f271,f272,f273
  f275: plane 51.31x1mm, normal (0,1,0), area 51.3mm2, adj f0,f77,f95,f280
  f276: plane 20.23x1mm, normal (0,-1,0), area 20.2mm2, adj f0,f77,f277,f280
  f277: plane 11.43x1mm, normal (-1,0,0), area 11.4mm2, adj f66,f77,f276,f280
  f278: plane 11.43x1mm, normal (1,0,0), area 11.4mm2, adj f66,f77,f279,f280
  f279: plane 20.23x1mm, normal (0,-1,0), area 20.2mm2, adj f77,f95,f278,f280
  f280: plane 51.31x13.84mm, normal (0,0,1), area 132.6mm2, adj f0,f66,f95,f275,f276,f277,f278,f279
  f281: plane 11.43x1mm, normal (0,1,0), area 11.4mm2, adj f1,f77,f282,f286
  f282: plane 20.23x1mm, normal (1,0,0), area 20.2mm2, adj f0,f77,f281,f286
  f283: plane 51.31x1mm, normal (-1,0,0), area 51.3mm2, adj f0,f77,f109,f286
  f284: plane 20.23x1mm, normal (1,0,0), area 20.2mm2, adj f77,f109,f285,f286
  f285: plane 11.43x1mm, normal (0,-1,0), area 11.4mm2, adj f1,f77,f284,f286
  f286: plane 51.31x13.84mm, normal (0,0,1), area 132.6mm2, adj f0,f1,f109,f281,f282,f283,f284,f285
  f287: plane 11.43x1mm, normal (0,-1,0), area 11.4mm2, adj f56,f77,f288,f292
  f288: plane 20.23x1mm, normal (-1,0,0), area 20.2mm2, adj f77,f123,f287,f292
  f289: plane 51.31x1mm, normal (1,0,0), area 51.3mm2, adj f77,f95,f123,f292
  f290: plane 20.23x1mm, normal (-1,0,0), area 20.2mm2, adj f77,f95,f291,f292
  f291: plane 11.43x1mm, normal (0,1,0), area 11.4mm2, adj f56,f77,f290,f292
  f292: plane 51.31x13.84mm, normal (0,0,1), area 132.6mm2, adj f56,f95,f123,f287,f288,f289,f290,f291
  f293: plane 11.43x1mm, normal (-1,0,0), area 11.4mm2, adj f46,f77,f294,f298
  f294: plane 20.23x1mm, normal (0,1,0), area 20.2mm2, adj f77,f109,f293,f298
  f295: plane 51.31x1mm, normal (0,-1,0), area 51.3mm2, adj f77,f109,f123,f298
  f296: plane 20.23x1mm, normal (0,1,0), area 20.2mm2, adj f77,f123,f297,f298
  f297: plane 11.43x1mm, normal (1,0,0), area 11.4mm2, adj f46,f77,f296,f298
  f298: plane 51.31x13.84mm, normal (0,0,1), area 132.6mm2, adj f46,f109,f123,f293,f294,f295,f296,f297
PART D: same geometry as B
PLACE A rot(axis=(0,1,0),180deg) t=(1.49,1.44,22.49)mm
PLACE B t=(-9.99,1.57,4.09)mm
PLACE C t=(1.36,1.57,3.49)mm
PLACE D t=(1.36,12.92,4.09)mm
MATE fastened C.f71 <-> A.f42  axis (0,0,1) through (1.36,19.57,21.49)mm
MATE fastened D.f1 <-> C.f23  axis (0,0,-1) through (1.36,12.92,4.09)mm
MATE fastened C.f25 <-> B.f1  axis (0,0,1) through (-9.99,1.57,4.09)mm
